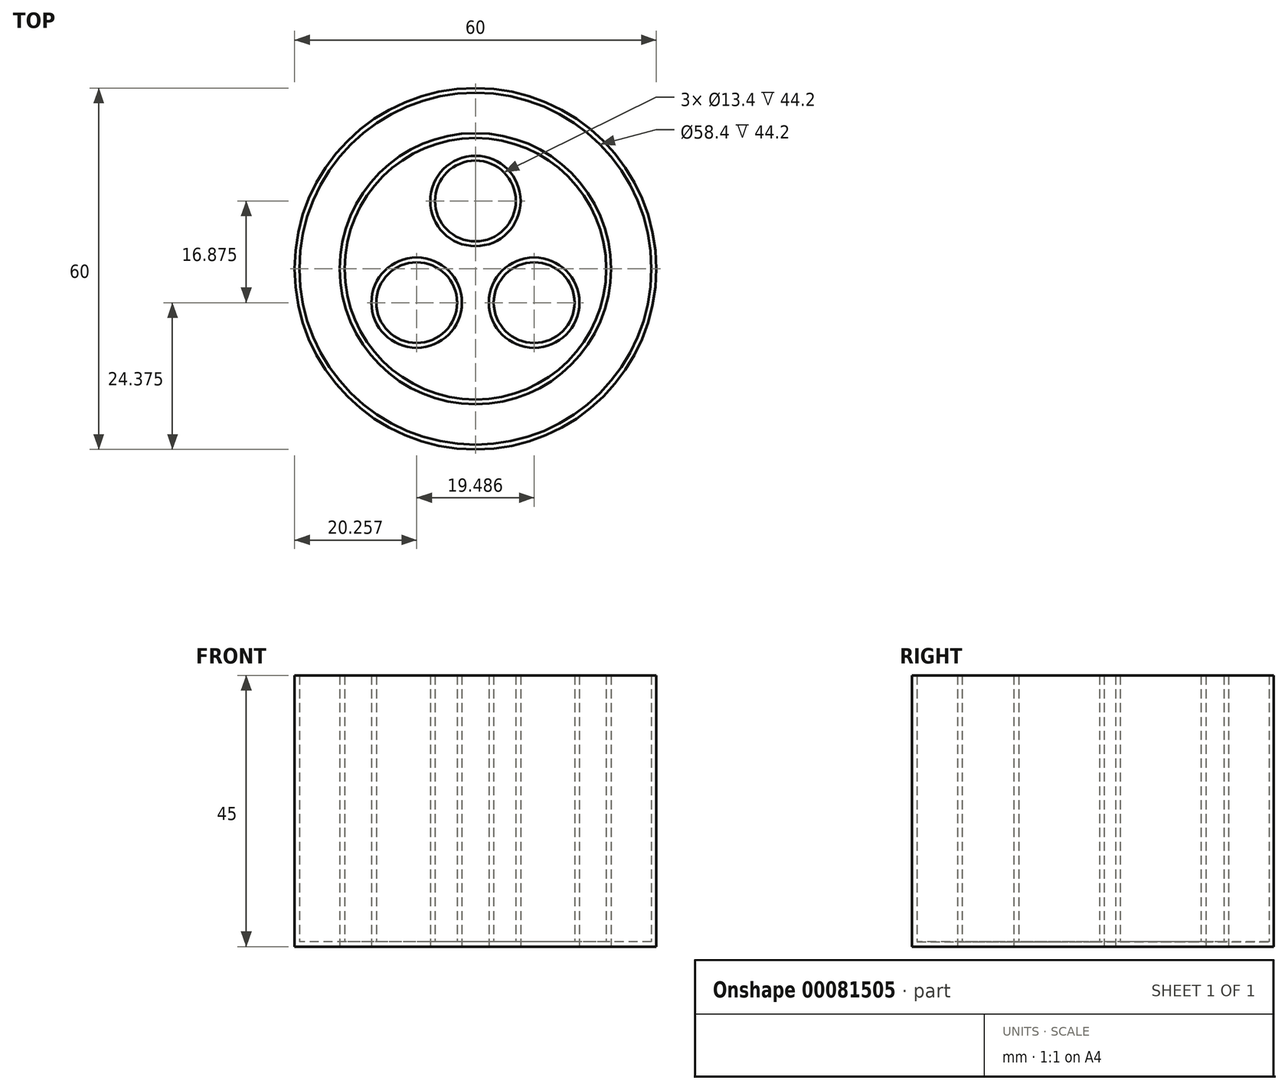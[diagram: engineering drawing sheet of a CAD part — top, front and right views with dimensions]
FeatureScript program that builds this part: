
annotation { "Feature Type Name" : "Feature", "Feature Type Description" : "" }
export const myFeature = defineFeature(function(context is Context, id is Id, definition is map)
    precondition{}
    {
        {
            var Q0;
            Q0=qCreatedBy(makeId("Top.planeOp"),FACE);
            var sketch = newSketch(context, id + "F0", { "sketchPlane" : qUnion([Q0])});
            skCircle(sketch, "E0", {"center": v(0, 0) * mm, "radius": 30 * mm});
            skCircle(sketch, "E1", {"center": v(0, 0) * mm, "radius": 22.5 * mm});
            skLineSegment(sketch, "E2", {"start": v(0, 0) * mm, "end": v(0, 22.5) * mm, "construction": true});
            skCircle(sketch, "E3", {"center": v(0, 11.25) * mm, "radius": 7.5 * mm});
            skCircle(sketch, "E4.1.0", {"center": v(-9.74, -5.62) * mm, "radius": 7.5 * mm});
            skCircle(sketch, "E4.2.0", {"center": v(9.74, -5.63) * mm, "radius": 7.5 * mm});
            skSolve(sketch);
        }
        {
            var Q0;
            Q0=makeQuery(id+"F0.imprint","IMPRINT",FACE,{"disambiguationData":[TD([[makeQuery(id+"F0.imprint","IMPRINT",EDGE,{"derivedFrom":sQuery(id+"F0.wireOp",EDGE,"E3")}),1.0]])]});
            var Q1;
            Q1=makeQuery(id+"F0.imprint","IMPRINT",FACE,{"disambiguationData":[TD([[makeQuery(id+"F0.imprint","IMPRINT",EDGE,{"derivedFrom":sQuery(id+"F0.wireOp",EDGE,"E4.2.0")}),1.0]])]});
            var Q2;
            Q2=makeQuery(id+"F0.imprint","IMPRINT",FACE,{"disambiguationData":[TD([[makeQuery(id+"F0.imprint","IMPRINT",EDGE,{"derivedFrom":sQuery(id+"F0.wireOp",EDGE,"E4.1.0")}),1.0]])]});
            var Q3;
            Q3=sQuery(id+"F0.wireOp",EDGE,"E3");
            var Q4;
            Q4=sQuery(id+"F0.wireOp",EDGE,"E4.2.0");
            var Q5;
            Q5=sQuery(id+"F0.wireOp",EDGE,"E4.1.0");
            extrude(context, id + "F1", {"entities" : qUnion([Q0, Q1, Q2]), "surfaceEntities" : qUnion([Q3, Q4, Q5]), "depth" : 45 * mm});
        }
        {
            var Q0;
            Q0=makeQuery(id+"F0.imprint","IMPRINT",FACE,{"disambiguationData":[TD([[makeQuery(id+"F0.imprint","IMPRINT",EDGE,{"derivedFrom":sQuery(id+"F0.wireOp",EDGE,"E4.1.0")}),1.0]])]});
            var Q1;
            Q1=makeQuery(id+"F0.imprint","IMPRINT",FACE,{"disambiguationData":[TD([[makeQuery(id+"F0.imprint","IMPRINT",EDGE,{"derivedFrom":sQuery(id+"F0.wireOp",EDGE,"E3")}),1.0]])]});
            var Q2;
            Q2=makeQuery(id+"F0.imprint","IMPRINT",FACE,{"disambiguationData":[TD([[makeQuery(id+"F0.imprint","IMPRINT",EDGE,{"derivedFrom":sQuery(id+"F0.wireOp",EDGE,"E4.2.0")}),1.0]])]});
            var Q3;
            Q3=makeQuery(id+"F0.imprint","IMPRINT",FACE,{"disambiguationData":[TD([[makeQuery(id+"F0.imprint","IMPRINT",EDGE,{"derivedFrom":sQuery(id+"F0.wireOp",EDGE,"E1")}),1.0]])]});
            extrude(context, id + "F2", {"entities" : qUnion([Q0, Q1, Q2, Q3]), "depth" : 45 * mm});
        }
        {
            var Q0;
            Q0=makeQuery(id+"F0.imprint","IMPRINT",FACE,{"disambiguationData":[TD([[makeQuery(id+"F0.imprint","IMPRINT",EDGE,{"derivedFrom":sQuery(id+"F0.wireOp",EDGE,"E0")}),1.0]])]});
            var Q1;
            Q1=makeQuery(id+"F0.imprint","IMPRINT",FACE,{"disambiguationData":[TD([[makeQuery(id+"F0.imprint","IMPRINT",EDGE,{"derivedFrom":sQuery(id+"F0.wireOp",EDGE,"E1")}),1.0]])]});
            var Q2;
            Q2=makeQuery(id+"F0.imprint","IMPRINT",FACE,{"disambiguationData":[TD([[makeQuery(id+"F0.imprint","IMPRINT",EDGE,{"derivedFrom":sQuery(id+"F0.wireOp",EDGE,"E4.1.0")}),1.0]])]});
            var Q3;
            Q3=makeQuery(id+"F0.imprint","IMPRINT",FACE,{"disambiguationData":[TD([[makeQuery(id+"F0.imprint","IMPRINT",EDGE,{"derivedFrom":sQuery(id+"F0.wireOp",EDGE,"E3")}),1.0]])]});
            var Q4;
            Q4=makeQuery(id+"F0.imprint","IMPRINT",FACE,{"disambiguationData":[TD([[makeQuery(id+"F0.imprint","IMPRINT",EDGE,{"derivedFrom":sQuery(id+"F0.wireOp",EDGE,"E4.2.0")}),1.0]])]});
            extrude(context, id + "F3", {"entities" : qUnion([Q0, Q1, Q2, Q3, Q4]), "depth" : 45 * mm});
        }
        {
            var Q0;
            Q0=makeQuery(id+"F3.opExtrude","CAP_FACE",FACE,{"disambiguationData":[OSD([sQuery(id+"F0.wireOp",EDGE,"E0")])],"isStart":false});
            shell(context, id + "F4", {"entities" : qUnion([Q0]), "thickness" : 0.8 * mm});
        }
        {
            var Q0;
            Q0=makeQuery(id+"F2.opExtrude","CAP_FACE",FACE,{"disambiguationData":[OSD([sQuery(id+"F0.wireOp",EDGE,"E1")])],"isStart":false});
            shell(context, id + "F5", {"entities" : qUnion([Q0]), "thickness" : 0.8 * mm});
        }
        {
            var Q0;
            Q0=makeQuery(id+"F1.opExtrude","CAP_FACE",FACE,{"disambiguationData":[OSD([sQuery(id+"F0.wireOp",EDGE,"E4.1.0")])],"isStart":false});
            shell(context, id + "F6", {"entities" : qUnion([Q0]), "thickness" : 0.8 * mm});
        }
        {
            var Q0;
            Q0=makeQuery(id+"F1.opExtrude","CAP_FACE",FACE,{"disambiguationData":[OSD([sQuery(id+"F0.wireOp",EDGE,"E3")])],"isStart":false});
            shell(context, id + "F7", {"entities" : qUnion([Q0]), "thickness" : 0.8 * mm});
        }
        {
            var Q0;
            Q0=makeQuery(id+"F1.opExtrude","CAP_FACE",FACE,{"disambiguationData":[OSD([sQuery(id+"F0.wireOp",EDGE,"E4.2.0")])],"isStart":false});
            shell(context, id + "F8", {"entities" : qUnion([Q0]), "thickness" : 0.8 * mm});
        }
    });
